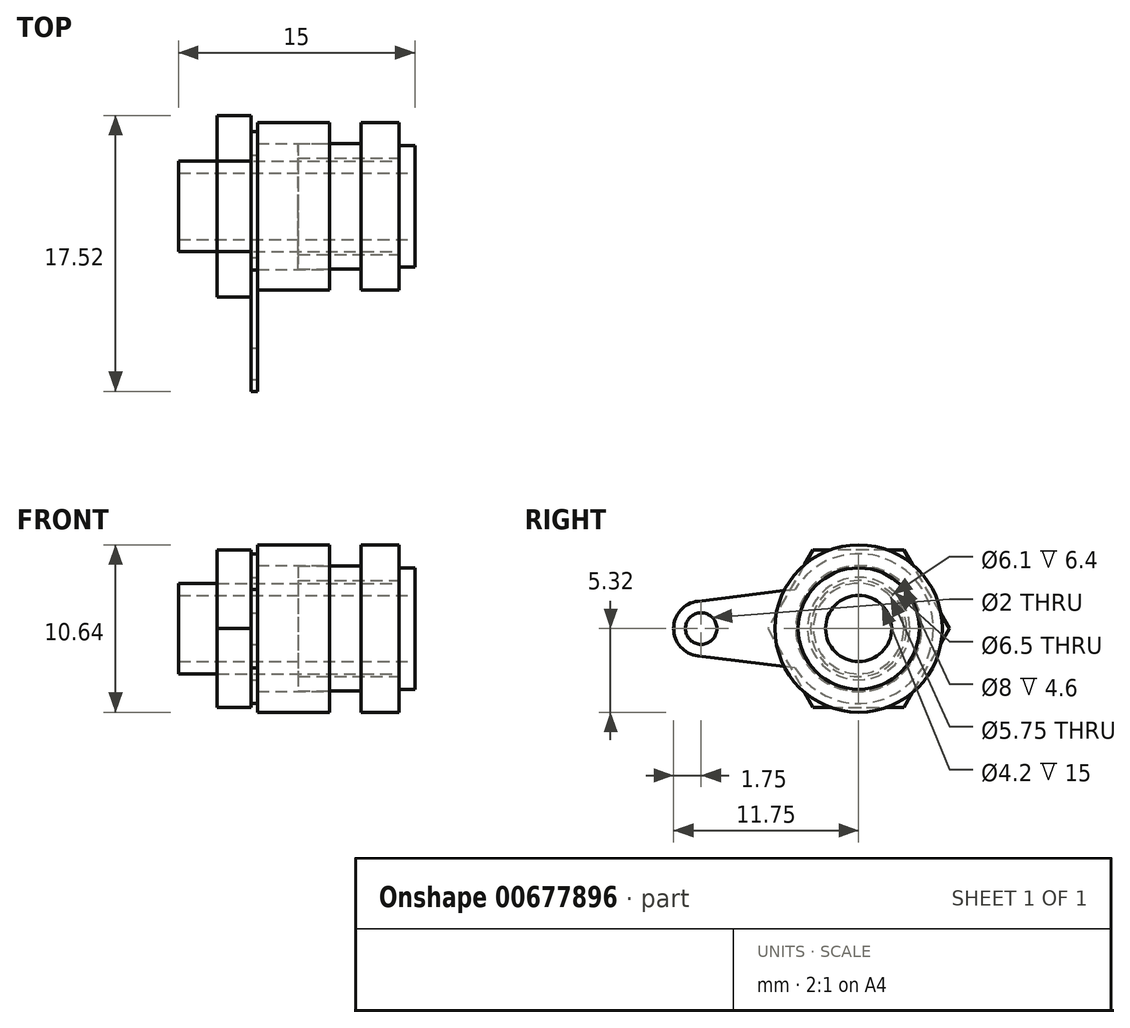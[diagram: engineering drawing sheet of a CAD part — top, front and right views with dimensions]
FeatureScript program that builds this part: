
annotation { "Feature Type Name" : "Feature", "Feature Type Description" : "" }
export const myFeature = defineFeature(function(context is Context, id is Id, definition is map)
    precondition{}
    {
        {
            var Q0;
            Q0=qCreatedBy(makeId("Right.planeOp"),FACE);
            var sketch = newSketch(context, id + "F0", { "sketchPlane" : qUnion([Q0])});
            skCircle(sketch, "E0", {"center": v(0, 0) * mm, "radius": 2.1 * mm});
            skCircle(sketch, "E1", {"center": v(0, 0) * mm, "radius": 2.88 * mm});
            skCircle(sketch, "E2", {"center": v(0, 0) * mm, "radius": 3.85 * mm});
            skSolve(sketch);
        }
        {
            var Q0;
            Q0=makeQuery(id+"F0.imprint","IMPRINT",FACE,{"disambiguationData":[TD([[makeQuery(id+"F0.imprint","IMPRINT",EDGE,{"derivedFrom":sQuery(id+"F0.wireOp",EDGE,"E0")}),-1.0]])]});
            extrude(context, id + "F1", {"entities" : qUnion([Q0]), "oppositeDirection" : true, "depth" : 15 * mm, "offsetDistance" : 25.4 * mm});
        }
        {
            var Q0;
            Q0 = qSketchRegion(id + "F0", true);
            extrude(context, id + "F2", {"entities" : qUnion([Q0]), "operationType" : NewBodyOperationType.ADD, "oppositeDirection" : true, "depth" : 1 * mm, "offsetDistance" : 25.4 * mm});
        }
        {
            var Q0;
            Q0=makeQuery(id+"F2.opExtrude","CAP_FACE",FACE,{"disambiguationData":[OSD([sQuery(id+"F0.wireOp",EDGE,"E1"),sQuery(id+"F0.wireOp",EDGE,"E2")])],"isStart":false});
            var sketch = newSketch(context, id + "F3", { "sketchPlane" : qUnion([Q0])});
            skCircle(sketch, "E3", {"center": v(0, 0) * mm, "radius": 3.98 * mm});
            skCircle(sketch, "E4", {"center": v(0, 0) * mm, "radius": 5.32 * mm});
            skCircle(sketch, "E5", {"center": v(0, 0) * mm, "radius": 3.05 * mm});
            skSolve(sketch);
        }
        {
            var Q0;
            Q0=makeQuery(id+"F3.imprint","IMPRINT",FACE,{"disambiguationData":[TD([[makeQuery(id+"F3.imprint","IMPRINT",EDGE,{"derivedFrom":sQuery(id+"F3.wireOp",EDGE,"E3")}),1.0]])]});
            var Q1;
            Q1=makeQuery(id+"F3.imprint","IMPRINT",FACE,{"disambiguationData":[TD([[makeQuery(id+"F3.imprint","IMPRINT",EDGE,{"derivedFrom":sQuery(id+"F3.wireOp",EDGE,"E5")}),-1.0]])]});
            extrude(context, id + "F4", {"entities" : qUnion([Q0, Q1]), "depth" : 6.4 * mm, "offsetDistance" : 25.4 * mm});
        }
        {
            var Q0;
            Q0 = qSketchRegion(id + "F3", true);
            extrude(context, id + "F5", {"entities" : qUnion([Q0]), "operationType" : NewBodyOperationType.ADD, "depth" : 2.4 * mm, "offsetDistance" : 25.4 * mm});
        }
        {
            var Q0;
            Q0=makeQuery(id+"F5.opExtrude","CAP_FACE",FACE,{"disambiguationData":[OSD([sQuery(id+"F3.wireOp",EDGE,"E3"),sQuery(id+"F3.wireOp",EDGE,"E4")])],"isStart":false});
            cPlane(context, id + "F6", {"entities" : qUnion([Q0]), "cplaneType" : CPlaneType.OFFSET, "offset" : 2 * mm, "width" : 152.4 * mm, "height" : 152.4 * mm});
        }
        {
            var Q0;
            Q0=qCreatedBy(id+"F6.planeOp",FACE);
            var sketch = newSketch(context, id + "F7", { "sketchPlane" : qUnion([Q0])});
            skCircle(sketch, "E6.0", {"center": v(0, 0) * mm, "radius": 5.32 * mm});
            skCircle(sketch, "E7", {"center": v(0, 0) * mm, "radius": 4 * mm});
            skSolve(sketch);
        }
        {
            var Q0;
            Q0 = qSketchRegion(id + "F7", true);
            extrude(context, id + "F8", {"entities" : qUnion([Q0]), "depth" : 4.6 * mm, "offsetDistance" : 25.4 * mm});
        }
        {
            var Q0;
            Q0=makeQuery(id+"F8.opExtrude","CAP_FACE",FACE,{"disambiguationData":[OSD([sQuery(id+"F7.wireOp",EDGE,"E6.0"),sQuery(id+"F7.wireOp",EDGE,"E7")])],"isStart":false});
            var sketch = newSketch(context, id + "F9", { "sketchPlane" : qUnion([Q0])});
            skCircle(sketch, "E8", {"center": v(0, 0) * mm, "radius": 3.25 * mm});
            skCircle(sketch, "E9", {"center": v(0, 0) * mm, "radius": 4.75 * mm});
            skLineSegment(sketch, "E10", {"start": v(4.04, -2.5) * mm, "end": v(10.21, -1.74) * mm});
            skLineSegment(sketch, "E11", {"start": v(10.21, 1.74) * mm, "end": v(4.04, 2.5) * mm});
            skCircle(sketch, "E12", {"center": v(10, 0) * mm, "radius": 1.75 * mm});
            skCircle(sketch, "E13", {"center": v(10, 0) * mm, "radius": 1 * mm});
            skSolve(sketch);
        }
        {
            var Q0;
            Q0 = qSketchRegion(id + "F9", true);
            extrude(context, id + "F10", {"entities" : qUnion([Q0]), "depth" : 0.4 * mm, "offsetDistance" : 25.4 * mm});
        }
        {
            var Q0;
            Q0=makeQuery(id+"F10.opExtrude","CAP_FACE",FACE,{"disambiguationData":[OSD([sQuery(id+"F9.wireOp",EDGE,"E8"),sQuery(id+"F9.wireOp",EDGE,"E9"),sQuery(id+"F9.wireOp",EDGE,"E10"),sQuery(id+"F9.wireOp",EDGE,"E11"),sQuery(id+"F9.wireOp",EDGE,"E12"),sQuery(id+"F9.wireOp",EDGE,"E13")])],"isStart":false});
            var sketch = newSketch(context, id + "F11", { "sketchPlane" : qUnion([Q0])});
            skCircle(sketch, "E14.cCircle", {"center": v(0, 0) * mm, "radius": 5 * mm, "construction": true});
            skLineSegment(sketch, "E14.0", {"start": v(2.89, 5) * mm, "end": v(5.77, 0) * mm});
            skLineSegment(sketch, "E14.1", {"start": v(5.77, 0) * mm, "end": v(2.89, -5) * mm});
            skLineSegment(sketch, "E14.2", {"start": v(2.89, -5) * mm, "end": v(-2.89, -5) * mm});
            skLineSegment(sketch, "E14.3", {"start": v(-2.89, -5) * mm, "end": v(-5.77, 0) * mm});
            skLineSegment(sketch, "E14.4", {"start": v(-5.77, 0) * mm, "end": v(-2.89, 5) * mm});
            skLineSegment(sketch, "E14.5", {"start": v(-2.89, 5) * mm, "end": v(2.89, 5) * mm});
            skPoint(sketch, "E14.0.midPoint", {"position": v(4.33, 2.5) * mm});
            skCircle(sketch, "E15.0", {"center": v(0, 0) * mm, "radius": 2.88 * mm});
            skSolve(sketch);
        }
        {
            var Q0;
            Q0 = qSketchRegion(id + "F11", true);
            extrude(context, id + "F12", {"entities" : qUnion([Q0]), "depth" : 2.15 * mm, "offsetDistance" : 25.4 * mm});
        }
    });
